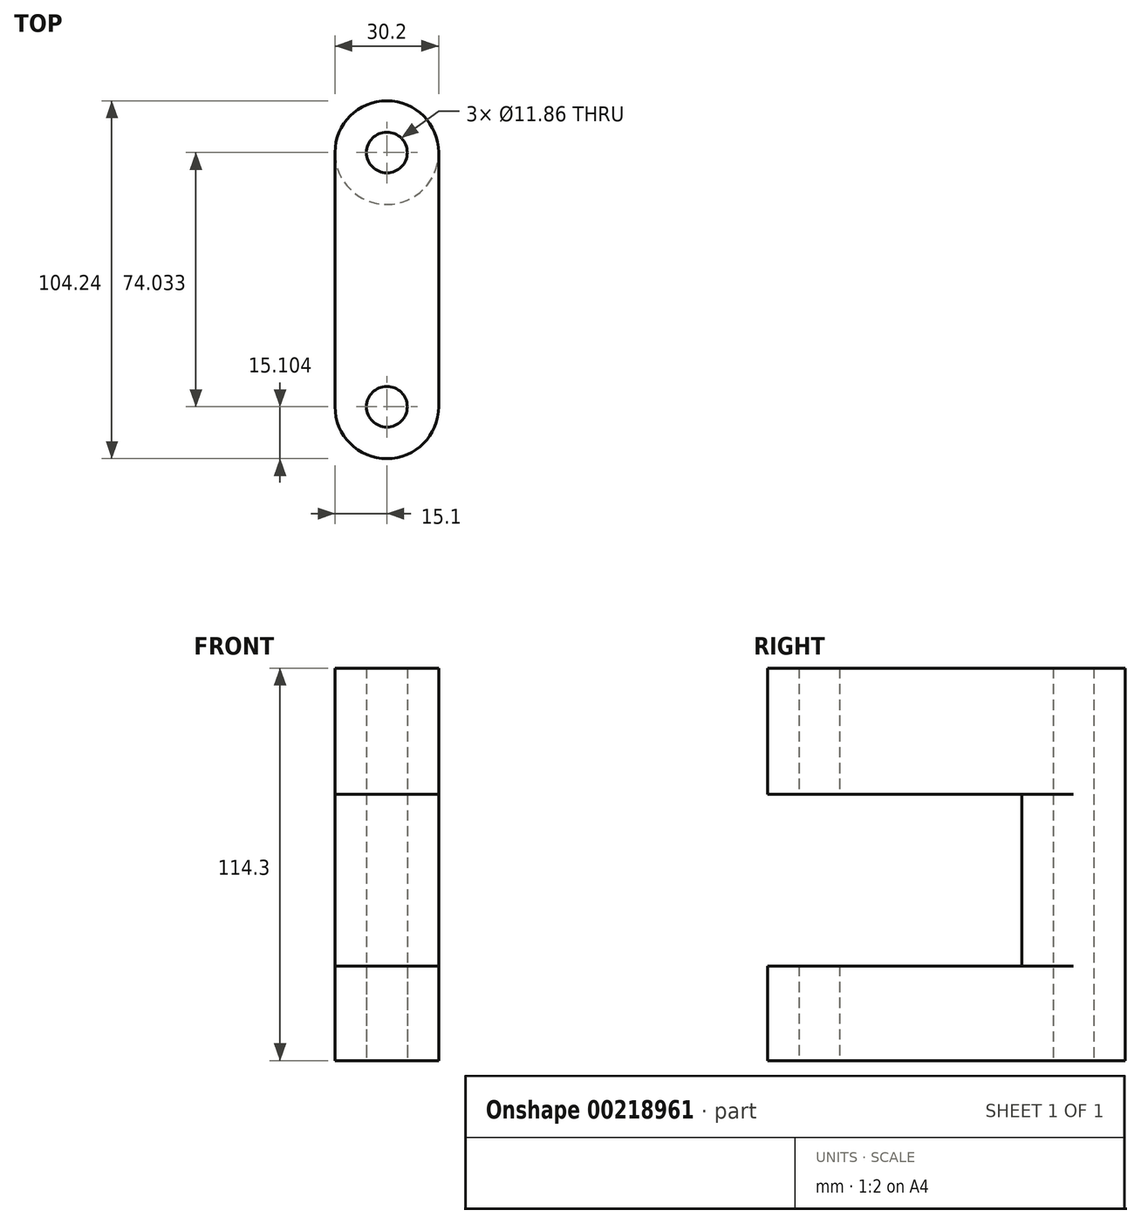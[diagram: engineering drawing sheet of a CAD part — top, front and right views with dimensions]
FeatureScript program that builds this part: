
annotation { "Feature Type Name" : "Feature", "Feature Type Description" : "" }
export const myFeature = defineFeature(function(context is Context, id is Id, definition is map)
    precondition{}
    {
        {
            var Q0;
            Q0=qCreatedBy(makeId("Top.planeOp"),FACE);
            var sketch = newSketch(context, id + "F0", { "sketchPlane" : qUnion([Q0])});
            skLineSegment(sketch, "E0.left", {"start": v(15.1, 37.02) * mm, "end": v(15.1, -37.02) * mm});
            skLineSegment(sketch, "E0.right", {"start": v(-15.1, 37.02) * mm, "end": v(-15.1, -37.02) * mm});
            skPoint(sketch, "E0.middle", {"position": v(0, 0) * mm});
            skCircle(sketch, "E1", {"center": v(0, 37.02) * mm, "radius": 15.1 * mm});
            skCircle(sketch, "E2", {"center": v(0, -37.02) * mm, "radius": 15.1 * mm});
            skCircle(sketch, "E3", {"center": v(0, 37.02) * mm, "radius": 5.93 * mm});
            skCircle(sketch, "E4", {"center": v(0, -37.02) * mm, "radius": 5.93 * mm});
            skSolve(sketch);
        }
        {
            var Q0;
            {var subQ0=sQuery(id+"F0.wireOp",EDGE,"E0.left");Q0=makeQuery(id+"F0.imprint","IMPRINT",FACE,{"disambiguationData":[TD([[makeQuery(id+"F0.imprint","IMPRINT",EDGE,{"derivedFrom":subQ0}),-1.0]])]});}
            var Q1;
            Q1=makeQuery(id+"F0.imprint","IMPRINT",FACE,{"disambiguationData":[TD([[makeQuery(id+"F0.imprint","IMPRINT",EDGE,{"derivedFrom":sQuery(id+"F0.wireOp",EDGE,"E4")}),-1.0]])]});
            var Q2;
            Q2=makeQuery(id+"F0.imprint","IMPRINT",FACE,{"disambiguationData":[TD([[makeQuery(id+"F0.imprint","IMPRINT",EDGE,{"derivedFrom":sQuery(id+"F0.wireOp",EDGE,"E3")}),-1.0]])]});
            extrude(context, id + "F1", {"entities" : qUnion([Q0, Q1, Q2]), "depth" : 114.3 * mm});
        }
        {
            var Q0;
            Q0=makeQuery(id+"F1.opExtrude","SWEPT_FACE",FACE,{"disambiguationData":[OSD([sQuery(id+"F0.wireOp",EDGE,"E0.left")])]});
            var sketch = newSketch(context, id + "F2", { "sketchPlane" : qUnion([Q0])});
            skLineSegment(sketch, "E5.bottom", {"start": v(55.48, 77.53) * mm, "end": v(-55.48, 77.53) * mm});
            skLineSegment(sketch, "E5.top", {"start": v(55.48, 27.53) * mm, "end": v(-55.48, 27.53) * mm});
            skLineSegment(sketch, "E5.left", {"start": v(55.48, 77.53) * mm, "end": v(55.48, 27.53) * mm});
            skLineSegment(sketch, "E5.right", {"start": v(-55.48, 77.53) * mm, "end": v(-55.48, 27.53) * mm});
            skPoint(sketch, "E5.middle", {"position": v(0, 52.53) * mm});
            skSolve(sketch);
        }
        {
            var Q0;
            {var subQ0=sQuery(id+"F2.wireOp",EDGE,"E5.bottom");var subQ1=sQuery(id+"F0.wireOp",EDGE,"E0.left");var subQ2=makeQuery(id+"F1.opExtrude","SWEPT_EDGE",EDGE,{"disambiguationData":[OSD([subQ1,sQuery(id+"F0.wireOp",EDGE,"E1")])]});var subQ3=makeQuery(id+"F2.imprint","INTERSECT",VERTEX,{"derivedFrom":[subQ2,subQ0]});Q0=makeQuery(id+"F2.imprint","IMPRINT",FACE,{"disambiguationData":[TD([[makeQuery(id+"F2.imprint","IMPRINT",EDGE,{"disambiguationData":[TD([[subQ3,-1.0]])],"derivedFrom":subQ0}),1.0]])]});}
            var Q1;
            {var subQ0=sQuery(id+"F2.wireOp",EDGE,"E5.right");Q1=makeQuery(id+"F2.imprint","IMPRINT",FACE,{"disambiguationData":[TD([[makeQuery(id+"F2.imprint","IMPRINT",EDGE,{"derivedFrom":subQ0}),1.0]])]});}
            var Q2;
            {var subQ0=sQuery(id+"F2.wireOp",EDGE,"E5.left");Q2=makeQuery(id+"F2.imprint","IMPRINT",FACE,{"disambiguationData":[TD([[makeQuery(id+"F2.imprint","IMPRINT",EDGE,{"derivedFrom":subQ0}),-1.0]])]});}
            extrude(context, id + "F3", {"entities" : qUnion([Q0, Q1, Q2]), "operationType" : NewBodyOperationType.REMOVE, "endBound" : BoundingType.THROUGH_ALL, "oppositeDirection" : true, "depth" : 25.4 * mm});
        }
        {
            var Q0;
            Q0=makeQuery(id+"F0.imprint","IMPRINT",FACE,{"disambiguationData":[TD([[makeQuery(id+"F0.imprint","IMPRINT",EDGE,{"derivedFrom":sQuery(id+"F0.wireOp",EDGE,"E3")}),-1.0]])]});
            var Q1;
            Q1=makeQuery(id+"F3.boolean.opBoolean","COPY",FACE,{"derivedFrom":makeQuery(id+"F3.opExtrude","SWEPT_FACE",FACE,{"disambiguationData":[OSD([sQuery(id+"F2.wireOp",EDGE,"E5.bottom")])]})});
            var Q2;
            Q2=makeQuery(id+"F3.boolean.opBoolean","SPLIT",BODY,{"disambiguationData":[OD(1.0)],"derivedFrom":makeQuery(id+"F1.opExtrude","SWEPT_BODY",BODY,{"disambiguationData":[OSD([sQuery(id+"F0.wireOp",EDGE,"E0.left"),sQuery(id+"F0.wireOp",EDGE,"E0.right"),sQuery(id+"F0.wireOp",EDGE,"E1"),sQuery(id+"F0.wireOp",EDGE,"E2"),sQuery(id+"F0.wireOp",EDGE,"E3"),sQuery(id+"F0.wireOp",EDGE,"E4")])]})});
            extrude(context, id + "F4", {"entities" : qUnion([Q0]), "operationType" : NewBodyOperationType.ADD, "endBoundEntityFace" : qUnion([Q1]), "endBoundEntityBody" : qUnion([Q2]), "depth" : 81.03 * mm});
        }
    });
